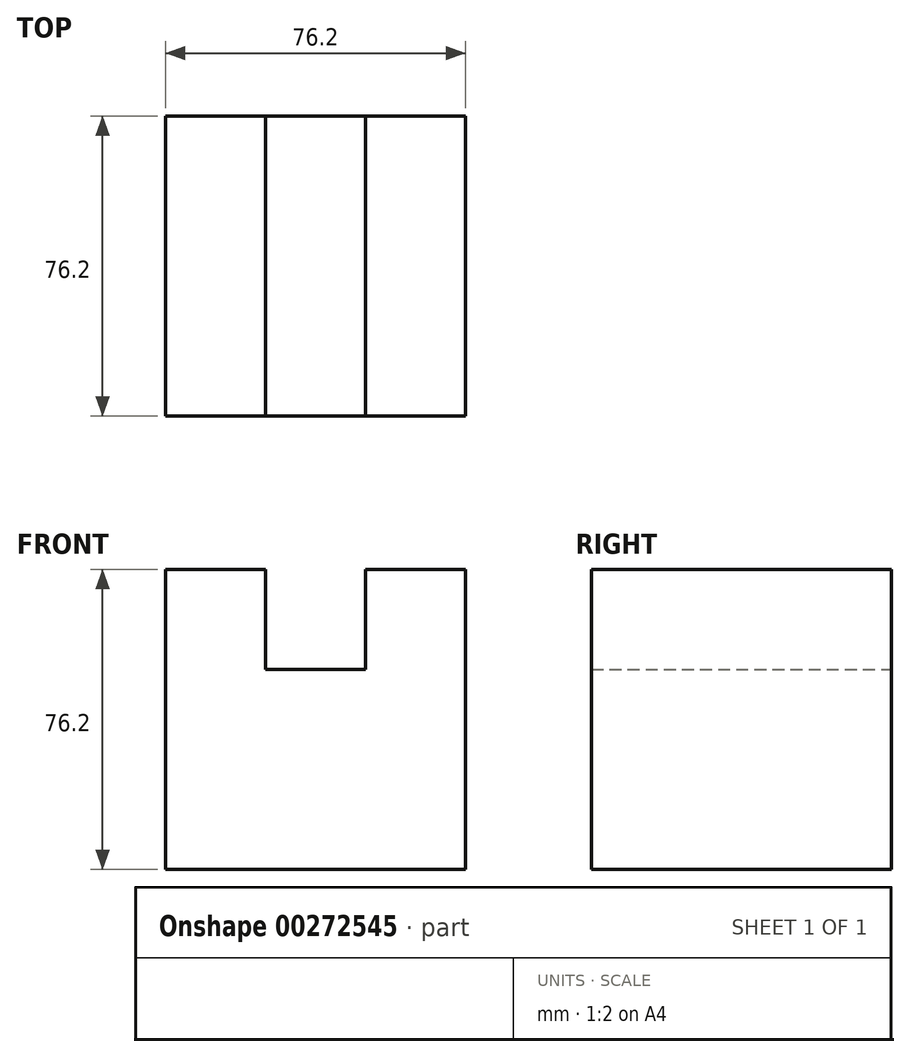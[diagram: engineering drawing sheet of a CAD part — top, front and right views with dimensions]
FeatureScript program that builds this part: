
annotation { "Feature Type Name" : "Feature", "Feature Type Description" : "" }
export const myFeature = defineFeature(function(context is Context, id is Id, definition is map)
    precondition{}
    {
        {
            var Q0;
            Q0=qCreatedBy(makeId("Front.planeOp"),FACE);
            var sketch = newSketch(context, id + "F0", { "sketchPlane" : qUnion([Q0])});
            skLineSegment(sketch, "E0", {"start": v(0, 0) * mm, "end": v(0, 76.2) * mm});
            skLineSegment(sketch, "E1", {"start": v(0, 76.2) * mm, "end": v(25.4, 76.2) * mm});
            skLineSegment(sketch, "E2", {"start": v(25.4, 76.2) * mm, "end": v(25.4, 50.8) * mm});
            skLineSegment(sketch, "E3", {"start": v(25.4, 50.8) * mm, "end": v(50.8, 50.8) * mm});
            skLineSegment(sketch, "E4", {"start": v(50.8, 50.8) * mm, "end": v(50.8, 76.2) * mm});
            skLineSegment(sketch, "E5", {"start": v(50.8, 76.2) * mm, "end": v(76.2, 76.2) * mm});
            skLineSegment(sketch, "E6", {"start": v(76.2, 76.2) * mm, "end": v(76.2, 50.8) * mm});
            skLineSegment(sketch, "E7", {"start": v(76.2, 50.8) * mm, "end": v(76.2, 0) * mm});
            skLineSegment(sketch, "E8", {"start": v(76.2, 0) * mm, "end": v(0, 0) * mm});
            skSolve(sketch);
        }
        {
            var Q0;
            Q0=makeQuery(id+"F0.imprint","IMPRINT",FACE,{"disambiguationData":[TD([[makeQuery(id+"F0.imprint","IMPRINT",EDGE,{"derivedFrom":sQuery(id+"F0.wireOp",EDGE,"E0")}),-1.0]])]});
            extrude(context, id + "F1", {"entities" : qUnion([Q0]), "depth" : 76.2 * mm});
        }
    });
